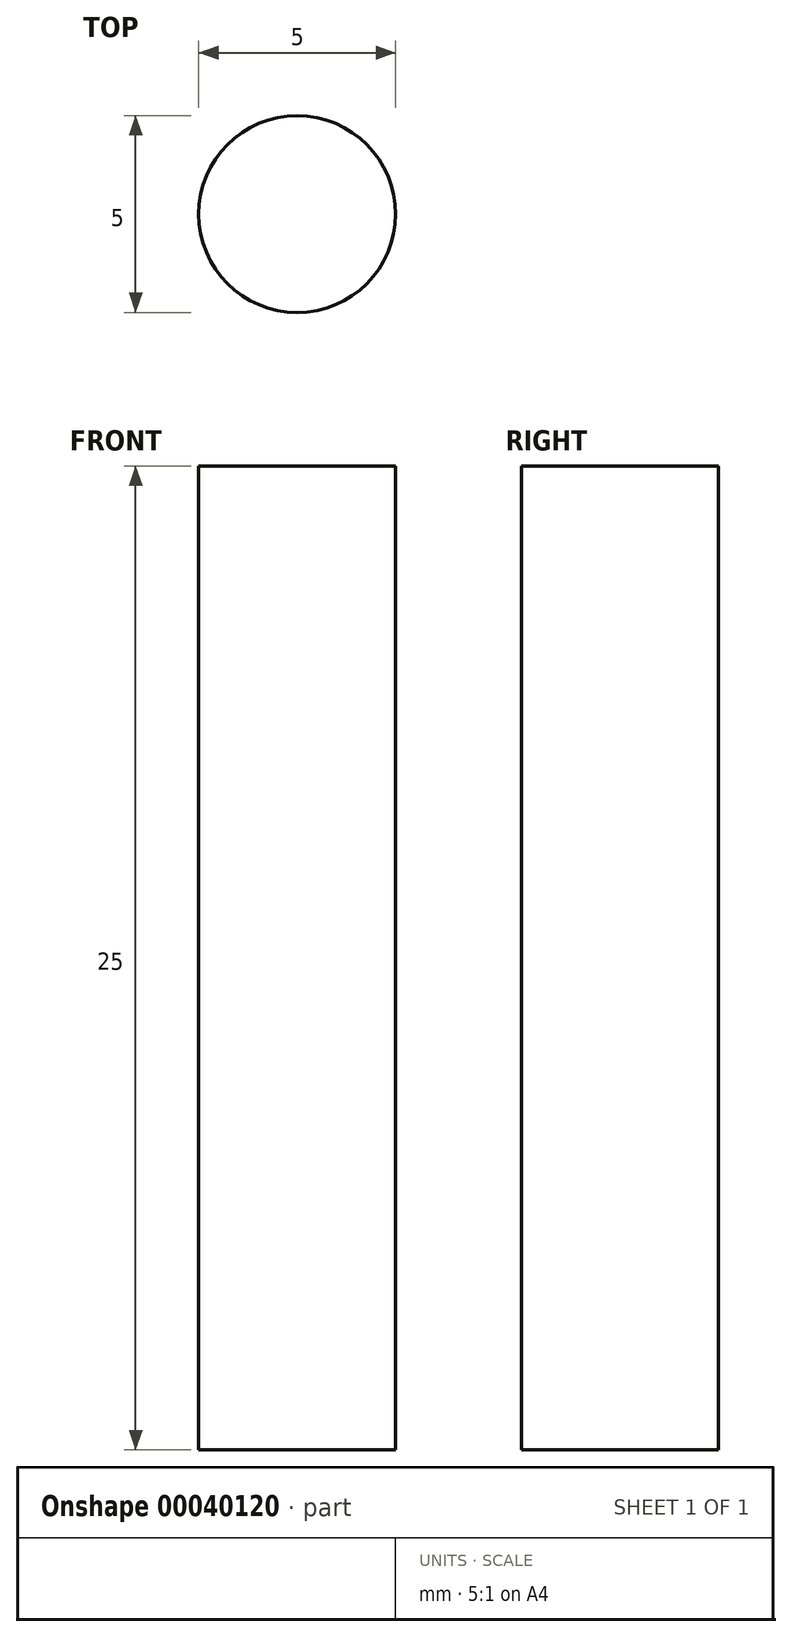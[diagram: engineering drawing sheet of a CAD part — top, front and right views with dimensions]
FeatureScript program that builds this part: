
annotation { "Feature Type Name" : "Feature", "Feature Type Description" : "" }
export const myFeature = defineFeature(function(context is Context, id is Id, definition is map)
    precondition{}
    {
        {
            var Q0;
            Q0=qCreatedBy(makeId("Top.planeOp"),FACE);
            var sketch = newSketch(context, id + "F0", { "sketchPlane" : qUnion([Q0])});
            skCircle(sketch, "E0", {"center": v(0, 0) * mm, "radius": 2.5 * mm});
            skSolve(sketch);
        }
        {
            var Q0;
            Q0=makeQuery(id+"F0.imprint","IMPRINT",FACE,{"disambiguationData":[TD([[makeQuery(id+"F0.imprint","IMPRINT",EDGE,{"derivedFrom":sQuery(id+"F0.wireOp",EDGE,"E0")}),1.0]])]});
            extrude(context, id + "F1", {"entities" : qUnion([Q0]), "depth" : 25 * mm});
        }
    });
